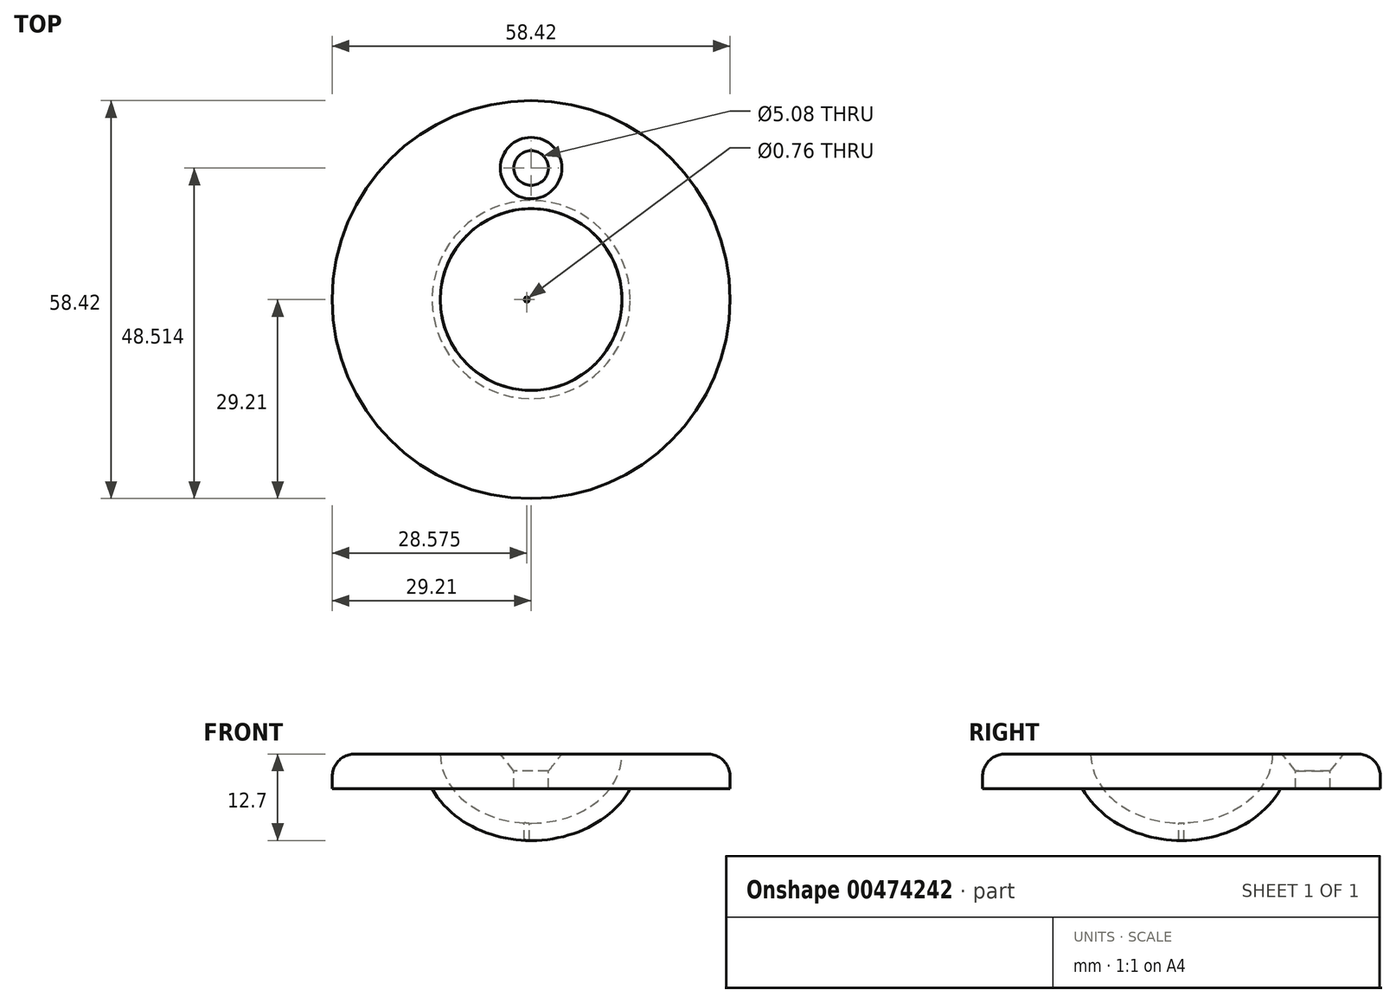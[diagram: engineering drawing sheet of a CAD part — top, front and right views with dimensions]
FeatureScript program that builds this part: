
annotation { "Feature Type Name" : "Feature", "Feature Type Description" : "" }
export const myFeature = defineFeature(function(context is Context, id is Id, definition is map)
    precondition{}
    {
        {
            var Q0;
            Q0=qCreatedBy(makeId("Top.planeOp"),FACE);
            var sketch = newSketch(context, id + "F0", { "sketchPlane" : qUnion([Q0])});
            skCircle(sketch, "E0", {"center": v(0, 0) * mm, "radius": 25.4 * mm});
            skCircle(sketch, "E1", {"center": v(0, 0) * mm, "radius": 12.7 * mm});
            skSolve(sketch);
        }
        {
            var Q0;
            Q0=qCreatedBy(makeId("Front.planeOp"),FACE);
            var sketch = newSketch(context, id + "F1", { "sketchPlane" : qUnion([Q0])});
            skEllipse(sketch, "E2", {"center": v(0, 0) * mm, "majorRadius": 13.34 * mm, "minorRadius": 10.16 * mm, "majorAxis": v(-1, 0)});
            skEllipse(sketch, "E3", {"center": v(0, 0) * mm, "majorRadius": 15.88 * mm, "minorRadius": 12.7 * mm, "majorAxis": v(-1, 0)});
            skLineSegment(sketch, "E4.bottom", {"start": v(0, 0) * mm, "end": v(29.21, 0) * mm});
            skLineSegment(sketch, "E4.top", {"start": v(0, -5.08) * mm, "end": v(29.21, -5.08) * mm});
            skLineSegment(sketch, "E4.left", {"start": v(0, 0) * mm, "end": v(0, -5.08) * mm});
            skLineSegment(sketch, "E4.right", {"start": v(29.21, 0) * mm, "end": v(29.21, -5.08) * mm});
            skLineSegment(sketch, "E5", {"start": v(0, -10.16) * mm, "end": v(0, -12.7) * mm});
            skSolve(sketch);
        }
        {
            var Q0;
            {var subQ0=sQuery(id+"F1.wireOp",EDGE,"E5");Q0=makeQuery(id+"F1.imprint","IMPRINT",FACE,{"disambiguationData":[TD([[makeQuery(id+"F1.imprint","IMPRINT",EDGE,{"derivedFrom":subQ0}),1.0]])]});}
            var Q1;
            {var subQ5=sQuery(id+"F1.wireOp",EDGE,"E4.right");Q1=makeQuery(id+"F1.imprint","IMPRINT",FACE,{"disambiguationData":[TD([[makeQuery(id+"F1.imprint","IMPRINT",EDGE,{"derivedFrom":subQ5}),-1.0]])]});}
            var Q2;
            {var subQ0=sQuery(id+"F1.wireOp",EDGE,"E4.top");var subQ1=sQuery(id+"F1.wireOp",EDGE,"E2");var subQ2=makeQuery(id+"F1.imprint","INTERSECT",VERTEX,{"derivedFrom":[subQ1,subQ0]});Q2=makeQuery(id+"F1.imprint","IMPRINT",FACE,{"disambiguationData":[TD([[makeQuery(id+"F1.imprint","IMPRINT",EDGE,{"disambiguationData":[TD([[subQ2,-1.0]])],"derivedFrom":subQ1}),-1.0]])]});}
            var Q3;
            Q3=sQuery(id+"F1.wireOp",EDGE,"E4.left");
            revolve(context, id + "F2", {"entities" : qUnion([Q0, Q1, Q2]), "axis" : qUnion([Q3]), "revolveType" : RevolveType.FULL});
        }
        {
            var Q0;
            Q0=makeQuery(id+"F2.opRevolve","SWEPT_EDGE",EDGE,{"disambiguationData":[OSD([sQuery(id+"F1.wireOp",EDGE,"E4.bottom"),sQuery(id+"F1.wireOp",EDGE,"E4.right")])]});
            fillet(context, id + "F3", {"entities" : qUnion([Q0]), "radius" : 3.3 * mm, "tangentPropagation" : true, "allowEdgeOverflow" : false});
        }
        {
            var Q0;
            Q0=makeQuery(id+"F0.imprint","IMPRINT",FACE,{"disambiguationData":[TD([[makeQuery(id+"F0.imprint","IMPRINT",EDGE,{"derivedFrom":sQuery(id+"F0.wireOp",EDGE,"E0")}),1.0]])]});
            var sketch = newSketch(context, id + "F4", { "sketchPlane" : qUnion([Q0])});
            skPoint(sketch, "E6", {"position": v(0, 19.3) * mm});
            skSolve(sketch);
        }
        {
            var Q0;
            Q0=sQuery(id+"F4.wireOp",VERTEX,"E6");
            var Q1;
            Q1=makeQuery(id+"F2.opRevolve","SWEPT_BODY",BODY,{"disambiguationData":[OSD([sQuery(id+"F1.wireOp",EDGE,"E2"),sQuery(id+"F1.wireOp",EDGE,"E3"),sQuery(id+"F1.wireOp",EDGE,"E4.bottom"),sQuery(id+"F1.wireOp",EDGE,"E4.top"),sQuery(id+"F1.wireOp",EDGE,"E4.right"),sQuery(id+"F1.wireOp",EDGE,"E5")])]});
            hole(context, id + "F5", {"style" : HoleStyle.C_SINK, "endStyle" : HoleEndStyle.THROUGH, "holeDiameter" : 5.08 * mm, "cSinkDiameter" : 9.02 * mm, "cSinkAngle" : 76 * degree, "isTappedThrough" : true, "tappedDepth" : 12.7 * mm, "tapClearance" : 3, "locations" : qUnion([Q0]), "scope" : qUnion([Q1])});
        }
        {
            var Q0;
            Q0=makeQuery(id+"F0.imprint","IMPRINT",FACE,{"disambiguationData":[TD([[makeQuery(id+"F0.imprint","IMPRINT",EDGE,{"derivedFrom":sQuery(id+"F0.wireOp",EDGE,"E1")}),1.0]])]});
            var sketch = newSketch(context, id + "F6", { "sketchPlane" : qUnion([Q0])});
            skCircle(sketch, "E7", {"center": v(-0.64, 0) * mm, "radius": 0.5 * mm});
            skSolve(sketch);
        }
        {
            var Q0;
            Q0=sQuery(id+"F6.wireOp",VERTEX,"E7.center");
            var Q1;
            Q1=makeQuery(id+"F2.opRevolve","SWEPT_BODY",BODY,{"disambiguationData":[OSD([sQuery(id+"F1.wireOp",EDGE,"E2"),sQuery(id+"F1.wireOp",EDGE,"E3"),sQuery(id+"F1.wireOp",EDGE,"E4.bottom"),sQuery(id+"F1.wireOp",EDGE,"E4.top"),sQuery(id+"F1.wireOp",EDGE,"E4.right"),sQuery(id+"F1.wireOp",EDGE,"E5")])]});
            hole(context, id + "F7", {"style" : HoleStyle.SIMPLE, "endStyle" : HoleEndStyle.THROUGH, "holeDiameter" : 0.76 * mm, "isTappedThrough" : true, "tappedDepth" : 12.7 * mm, "tapClearance" : 3, "locations" : qUnion([Q0]), "scope" : qUnion([Q1])});
        }
    });
